# Revit family: ClosetMaid - ShelfTrack EVO - Adjustable Solid Wood Melamine Shelving w Hang Rod
name_source: partatom
category: Specialty Equipment
revit_build: Autodesk Revit 2018 (Build: 20190510_1515(x64)
units: mm (PartAtom-declared; Revit-internal decimal feet)

## family parameters
Always vertical = Yes
Cut with Voids When Loaded = No
Part Type = Normal
Room Calculation Point = No
Round Connector Dimension = Use Diameter
Shared = No
Work Plane-Based = No

## types (2) — shared parameters
Description = Solid Wood Adjustable Shelving
Keynote = 10 57 00
Lower Shelf Height = 3' - 6"
Manufacturer = ClosetMaid
Maximum Standards Spacing = 2' - 6"
Shelf Depth = 1' - 2"
Shelf Material = White Finish
Standards Length = 7' - 0"
Support Material = White Finish
Type Comments = 5/8'' Solid Melamine Shelving
URL = www.ClosetMaidPro.com

## per-type parameters (varying)
| type | Double Hang | Upper Shelf Height |
| 84" Single Hang - 14" Depth | No | 5' - 10" |
| 84" Double Hang - 14" Depth | Yes | 7' - 0" |

## geometry (parser evidence)
native form markers: Sweep x19
no freeform markers — native parametric forms only
